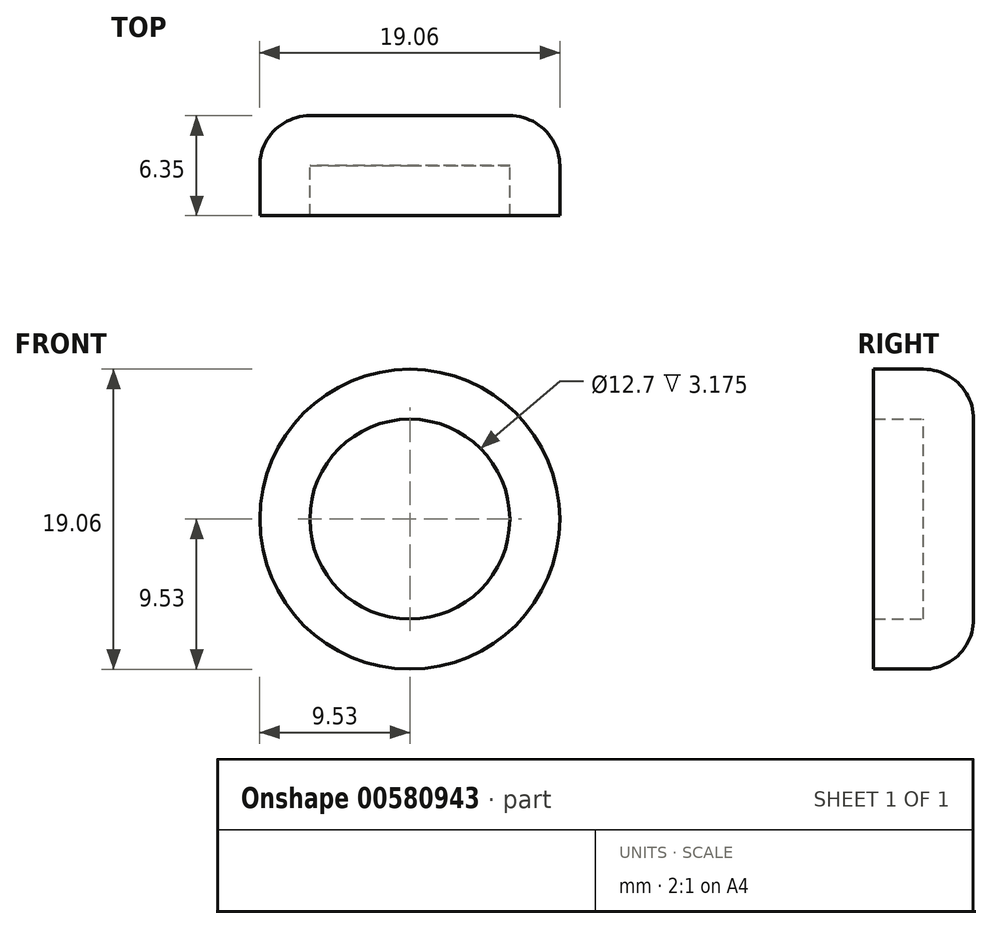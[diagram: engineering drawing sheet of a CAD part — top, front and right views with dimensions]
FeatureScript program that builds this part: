
annotation { "Feature Type Name" : "Feature", "Feature Type Description" : "" }
export const myFeature = defineFeature(function(context is Context, id is Id, definition is map)
    precondition{}
    {
        {
            var Q0;
            Q0=qCreatedBy(makeId("Front.planeOp"),FACE);
            var sketch = newSketch(context, id + "F0", { "sketchPlane" : qUnion([Q0])});
            skCircle(sketch, "E0", {"center": v(0, 0) * mm, "radius": 9.52 * mm});
            skCircle(sketch, "E1", {"center": v(0, 0) * mm, "radius": 6.35 * mm});
            skSolve(sketch);
        }
        {
            var Q0;
            Q0=makeQuery(id+"F0.imprint","IMPRINT",FACE,{"disambiguationData":[TD([[makeQuery(id+"F0.imprint","IMPRINT",EDGE,{"derivedFrom":sQuery(id+"F0.wireOp",EDGE,"E0")}),1.0]])]});
            extrude(context, id + "F1", {"entities" : qUnion([Q0]), "depth" : 6.35 * mm, "offsetDistance" : 25.4 * mm});
        }
        {
            var Q0;
            Q0=makeQuery(id+"F0.imprint","IMPRINT",FACE,{"disambiguationData":[TD([[makeQuery(id+"F0.imprint","IMPRINT",EDGE,{"derivedFrom":sQuery(id+"F0.wireOp",EDGE,"E1")}),1.0]])]});
            extrude(context, id + "F2", {"entities" : qUnion([Q0]), "operationType" : NewBodyOperationType.ADD, "depth" : 3.17 * mm, "offsetDistance" : 25.4 * mm});
        }
        {
            var Q0;
            Q0=makeQuery(id+"F1.opExtrude","CAP_EDGE",EDGE,{"disambiguationData":[OSD([sQuery(id+"F0.wireOp",EDGE,"E0")])],"isStart":true});
            fillet(context, id + "F3", {"entities" : qUnion([Q0]), "radius" : 3.17 * mm, "tangentPropagation" : true, "allowEdgeOverflow" : false});
        }
    });
